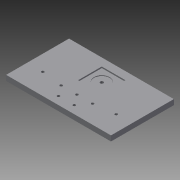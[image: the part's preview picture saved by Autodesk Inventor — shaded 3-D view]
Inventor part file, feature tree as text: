
AUTODESK INVENTOR PART (.ipt)
format: ipt  version: 2013 (Build 170138000, 138)  size: 125,440 bytes
history: native  units: in
note: dims shown in document units (in); Inventor stores cm internally (conversion verified against a paired STEP export)
features: sketch x6, extrude x4, hole x2
ambient origin geometry x8: Origin, YZ Plane, XZ Plane, XY Plane, X Axis, Y Axis, Z Axis, Center Point
bodies: Solid1 (feature_tree)
feature tree (12):
  extrude  "Extrusion1"  Depth=6.0in
  extrude  "Extrusion2"  Depth=2.25in
  extrude  "Extrusion3"  Depth=3.875in
  extrude  "Extrusion4"  Depth=0.75in
  hole  "Hole1"  [1 undecoded]
  hole  "Hole5"  [1 undecoded]
  sketch  "Sketch1"  dims[d0=10.0in d1=6.0in]
  sketch  "Sketch2"  dims[d2=0.5in d3=0.0in d4=2.25in]
  sketch  "Sketch3"  dims[d6=2.25in d7=3.875in]
  sketch  "Sketch4"  dims[d8=3.875in d9=0.75in]
  sketch  "Sketch5"  dims[d10=0.125in d11=0.0in d12=1.5in]
  sketch  "Sketch10"  dims[d13=1.125in d14=1.125in d15=0.06in d16=0.0in d17=0.3in d18=0.06in d19=0.0in d20=2.0in d21=1.5in d22=1.5in d23=0.25in d24=0.75in d25=0.375in d26=0.25in d27=0.5635in d28=1.0in d29=0.8108in d67=1.5in d69=1.5in d70=0.75in d71=0.75in d72=5.0in d73=5.0in d74=0.75in d75=1.0in d76=0.25in d77=0.75in d78=0.375in d79=0.25in d80=0.5635in d81=1.0in d82=0.8108in]
note: 2 required parameter values undecoded (feature->parameter linkage not recoverable at this tier; creation-order binding heuristic only, values carry confidence <= 0.55)
